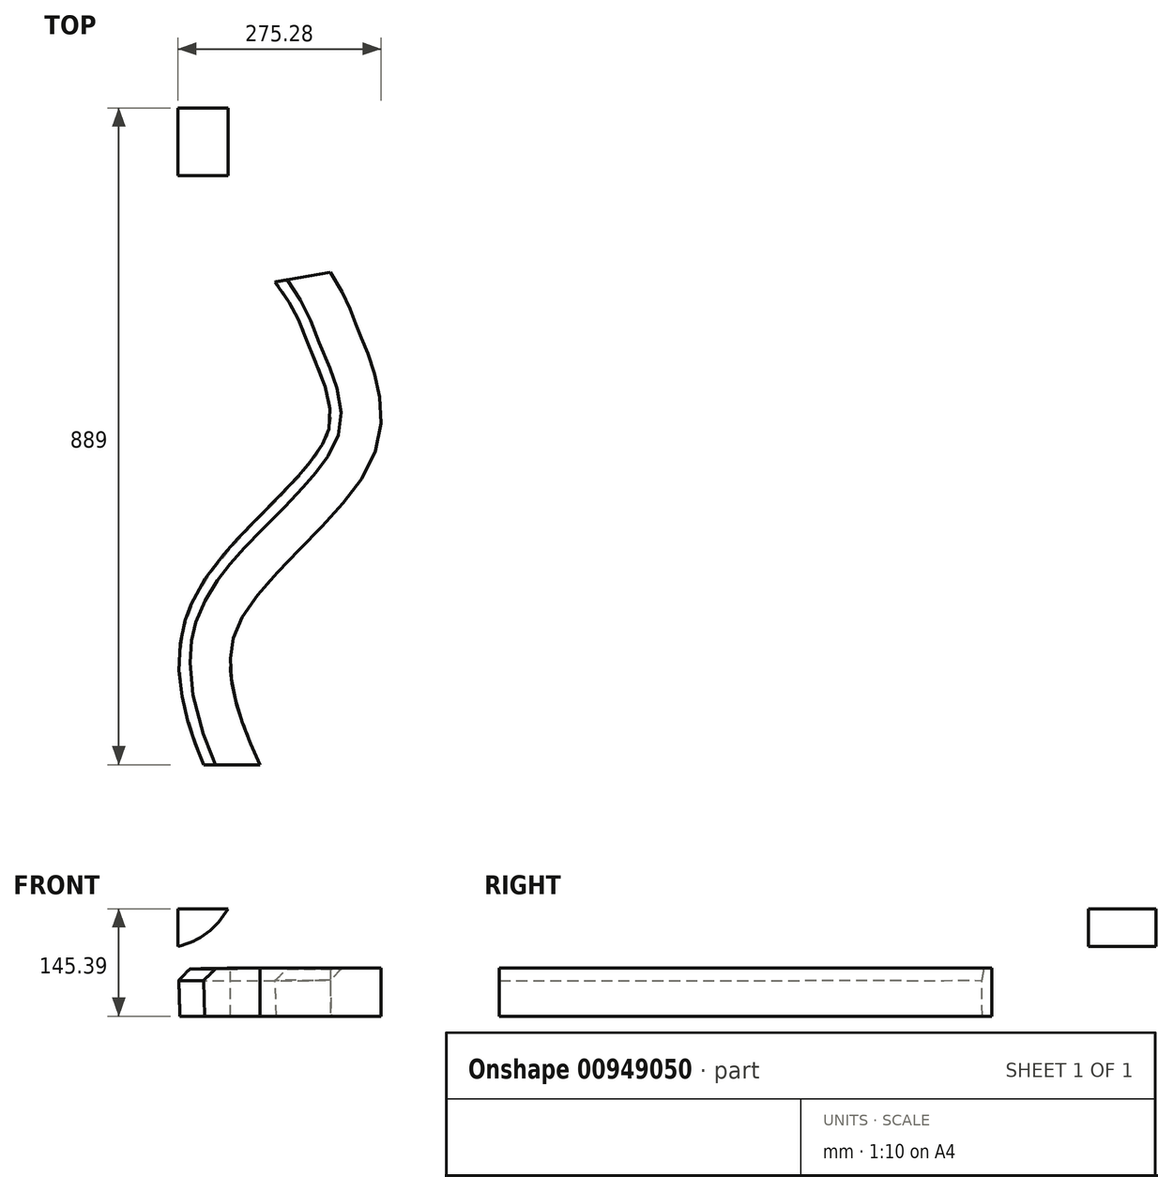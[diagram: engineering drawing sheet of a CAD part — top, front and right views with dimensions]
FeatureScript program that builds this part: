
annotation { "Feature Type Name" : "Feature", "Feature Type Description" : "" }
export const myFeature = defineFeature(function(context is Context, id is Id, definition is map)
    precondition{}
    {
        {
            var Q0;
            Q0=qCreatedBy(makeId("Front.planeOp"),FACE);
            var sketch = newSketch(context, id + "F0", { "sketchPlane" : qUnion([Q0])});
            skLineSegment(sketch, "E0", {"start": v(-39.68, -25.85) * mm, "end": v(-41.7, 37.89) * mm});
            skLineSegment(sketch, "E1", {"start": v(35, 39.07) * mm, "end": v(35, -25.85) * mm});
            skLineSegment(sketch, "E2", {"start": v(35, -25.85) * mm, "end": v(-39.68, -25.85) * mm});
            skLineSegment(sketch, "E3", {"start": v(-41.7, 37.89) * mm, "end": v(35, 39.07) * mm});
            skSolve(sketch);
        }
        {
            var Q0;
            Q0=qCreatedBy(makeId("Top.planeOp"),FACE);
            var sketch = newSketch(context, id + "F1", { "sketchPlane" : qUnion([Q0])});
            skFitSpline(sketch, "E4", {"points": [v(0, 0) * mm, v(-23.37, 201) * mm, v(159.54, 432.64) * mm, v(139.19, 573.68) * mm, v(96.29, 660.53) * mm], "startDerivative": vector(-288.3, 663.5) * mm, "endDerivative": vector(-423.12, 640.71) * mm});
            skSolve(sketch);
        }
        {
            var Q0;
            Q0=makeQuery(id+"F0.imprint","IMPRINT",FACE,{"disambiguationData":[TD([[makeQuery(id+"F0.imprint","IMPRINT",EDGE,{"derivedFrom":sQuery(id+"F0.wireOp",EDGE,"E0")}),-1.0]])]});
            var Q1;
            Q1=sQuery(id+"F0.wireOp",EDGE,"MDk4Yp86-zy5K-UsjP-L18l-sgq4i4sF3nPe");
            var Q2;
            Q2=sQuery(id+"F0.wireOp",EDGE,"E2");
            var Q3;
            Q3=sQuery(id+"F0.wireOp",EDGE,"E1");
            var Q4;
            Q4=sQuery(id+"F0.wireOp",EDGE,"eGxTR0Br-KlG4-qWNr-YCd2-uhovpcranKpS");
            var Q5;
            Q5=sQuery(id+"F0.wireOp",EDGE,"kHYyObB9-oVtn-0aYR-YO7h-cFjpTFSZa5Mj");
            var Q6;
            Q6=sQuery(id+"F0.wireOp",EDGE,"E0");
            var Q7;
            Q7=sQuery(id+"F0.wireOp",EDGE,"WQ7ID6j4-LOaI-OdNv-RJI2-kdR6agSTJ8xc");
            var Q8;
            Q8=sQuery(id+"F1.wireOp",EDGE,"E4");
            sweep(context, id + "F2", {"profiles" : qUnion([Q0]), "surfaceProfiles" : qUnion([Q1, Q2, Q3, Q4, Q5, Q6, Q7]), "path" : qUnion([Q8])});
        }
        {
            var Q0;
            Q0=qCreatedBy(makeId("Front.planeOp"),FACE);
            cPlane(context, id + "F3", {"entities" : qUnion([Q0]), "cplaneType" : CPlaneType.OFFSET, "offset" : 797.56 * mm, "oppositeDirection" : true, "width" : 152.4 * mm, "height" : 152.4 * mm});
        }
        {
            var Q0;
            Q0=makeQuery(id+"F2.opSweep","SWEPT_EDGE",EDGE,{"disambiguationData":[OSD([sQuery(id+"F0.wireOp",EDGE,"E0"),sQuery(id+"F0.wireOp",EDGE,"E3"),sQuery(id+"F1.wireOp",EDGE,"E4")])]});
            chamfer(context, id + "F4", {"entities" : qUnion([Q0]), "width" : 15.24 * mm, "tangentPropagation" : true});
        }
        {
            var Q0;
            Q0=qCreatedBy(id+"F3.planeOp",FACE);
            var sketch = newSketch(context, id + "F5", { "sketchPlane" : qUnion([Q0])});
            skLineSegment(sketch, "E5.bottom", {"start": v(-76.1, 119.54) * mm, "end": v(36.11, 119.54) * mm});
            skLineSegment(sketch, "E5.top", {"start": v(-76.1, 0) * mm, "end": v(36.11, 0) * mm});
            skLineSegment(sketch, "E5.left", {"start": v(-76.1, 119.54) * mm, "end": v(-76.1, 0) * mm});
            skLineSegment(sketch, "E5.right", {"start": v(36.11, 119.54) * mm, "end": v(36.11, 0) * mm});
            skSolve(sketch);
        }
        {
            var Q0;
            Q0=qCreatedBy(id+"F3.planeOp",FACE);
            cPlane(context, id + "F6", {"entities" : qUnion([Q0]), "cplaneType" : CPlaneType.OFFSET, "offset" : 25.4 * mm, "width" : 152.4 * mm, "height" : 152.4 * mm});
        }
        {
            var Q0;
            Q0=qCreatedBy(id+"F6.planeOp",FACE);
            var sketch = newSketch(context, id + "F7", { "sketchPlane" : qUnion([Q0])});
            skCircle(sketch, "E6", {"center": v(-97.51, 167.8) * mm, "radius": 101.47 * mm});
            skSolve(sketch);
        }
        {
            var Q0;
            Q0=makeQuery(id+"F7.imprint","IMPRINT",FACE,{"disambiguationData":[TD([[makeQuery(id+"F7.imprint","IMPRINT",EDGE,{"derivedFrom":sQuery(id+"F7.wireOp",EDGE,"E6")}),1.0]])]});
            var Q1;
            Q1=sQuery(id+"F7.wireOp",EDGE,"E6");
            extrude(context, id + "F8", {"entities" : qUnion([Q0]), "surfaceEntities" : qUnion([Q1]), "oppositeDirection" : true, "depth" : 116.84 * mm, "offsetDistance" : 25.4 * mm});
        }
        {
            var Q0;
            Q0=makeQuery(id+"F5.imprint","IMPRINT",FACE,{"disambiguationData":[TD([[makeQuery(id+"F5.imprint","IMPRINT",EDGE,{"derivedFrom":sQuery(id+"F5.wireOp",EDGE,"E5.bottom")}),-1.0]])]});
            extrude(context, id + "F9", {"entities" : qUnion([Q0]), "oppositeDirection" : true, "depth" : 177.8 * mm, "offsetDistance" : 25.4 * mm});
        }
        {
            var Q0;
            Q0=makeQuery(id+"F9.opExtrude","SWEPT_BODY",BODY,{"disambiguationData":[OSD([sQuery(id+"F5.wireOp",EDGE,"E5.bottom"),sQuery(id+"F5.wireOp",EDGE,"E5.top"),sQuery(id+"F5.wireOp",EDGE,"E5.left"),sQuery(id+"F5.wireOp",EDGE,"E5.right")])]});
            var Q1;
            Q1=makeQuery(id+"F8.opExtrude","SWEPT_BODY",BODY,{"disambiguationData":[OSD([sQuery(id+"F7.wireOp",EDGE,"E6")])]});
            var Q2;
            Q2=makeQuery(id+"F8.opExtrude","SWEPT_BODY",BODY,{"disambiguationData":[OSD([sQuery(id+"F7.wireOp",EDGE,"E6")])]});
            booleanBodies(context, id + "F10", {"operationType" : BooleanOperationType.INTERSECTION, "tools" : qUnion([Q0, Q1]), "targets" : qUnion([Q2])});
        }
    });
